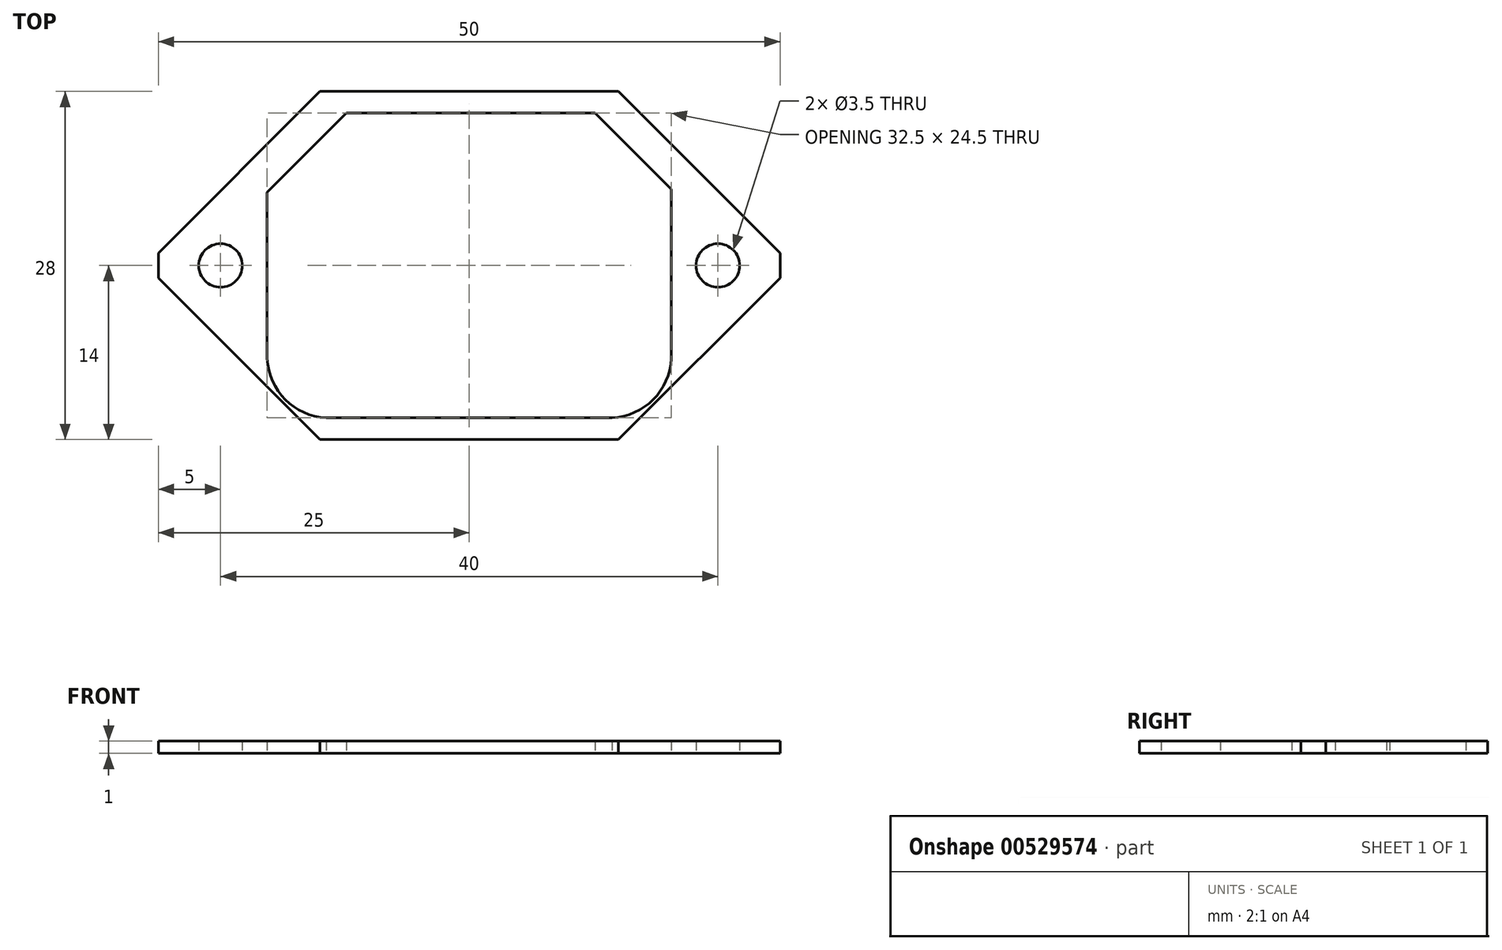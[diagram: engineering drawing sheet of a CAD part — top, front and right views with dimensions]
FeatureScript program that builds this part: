
annotation { "Feature Type Name" : "Feature", "Feature Type Description" : "" }
export const myFeature = defineFeature(function(context is Context, id is Id, definition is map)
    precondition{}
    {
        {
            var Q0;
            Q0=qCreatedBy(makeId("Top.planeOp"),FACE);
            var sketch = newSketch(context, id + "F0", { "sketchPlane" : qUnion([Q0])});
            skLineSegment(sketch, "E0.bottom", {"start": v(-9.88, 12.25) * mm, "end": v(10.12, 12.25) * mm});
            skLineSegment(sketch, "E0.top", {"start": v(-11.5, -12.25) * mm, "end": v(11.5, -12.25) * mm});
            skLineSegment(sketch, "E0.left", {"start": v(-16.25, 5.88) * mm, "end": v(-16.25, -7.5) * mm});
            skLineSegment(sketch, "E0.right", {"start": v(16.25, 6.12) * mm, "end": v(16.25, -7.5) * mm});
            skLineSegment(sketch, "E1.bottom", {"start": v(-12, 14) * mm, "end": v(12, 14) * mm});
            skLineSegment(sketch, "E1.top", {"start": v(-12, -14) * mm, "end": v(12, -14) * mm});
            skLineSegment(sketch, "E1.left", {"start": v(-25, 1) * mm, "end": v(-25, -1) * mm});
            skLineSegment(sketch, "E1.right", {"start": v(25, 1) * mm, "end": v(25, -1) * mm});
            skLineSegment(sketch, "E2", {"start": v(10.12, 12.25) * mm, "end": v(16.25, 6.12) * mm});
            skLineSegment(sketch, "E3", {"start": v(-16.25, 5.88) * mm, "end": v(-9.88, 12.25) * mm});
            skPoint(sketch, "E4.orphan", {"position": v(16.25, 12.25) * mm});
            skCircle(sketch, "E5", {"center": v(-20, 0) * mm, "radius": 1.75 * mm});
            skCircle(sketch, "E6", {"center": v(20, 0) * mm, "radius": 1.75 * mm});
            skLineSegment(sketch, "E7", {"start": v(-25, 1) * mm, "end": v(-12, 14) * mm});
            skLineSegment(sketch, "E8", {"start": v(12, 14) * mm, "end": v(25, 1) * mm});
            skLineSegment(sketch, "E9", {"start": v(-25, -1) * mm, "end": v(-12, -14) * mm});
            skLineSegment(sketch, "E10", {"start": v(25, -1) * mm, "end": v(12, -14) * mm});
            skArc(sketch, "E11", {"start": v(-16.25, -7.5) * mm, "mid": v(-14.8, -10.8) * mm, "end": v(-11.5, -12.25) * mm});
            skArc(sketch, "E12", {"start": v(11.5, -12.25) * mm, "mid": v(14.8, -10.8) * mm, "end": v(16.25, -7.5) * mm});
            skSolve(sketch);
        }
        {
            var Q0;
            Q0 = qSketchRegion(id + "F0", true);
            extrude(context, id + "F1", {"entities" : qUnion([Q0]), "depth" : 1 * mm, "offsetDistance" : 25 * mm});
        }
    });
